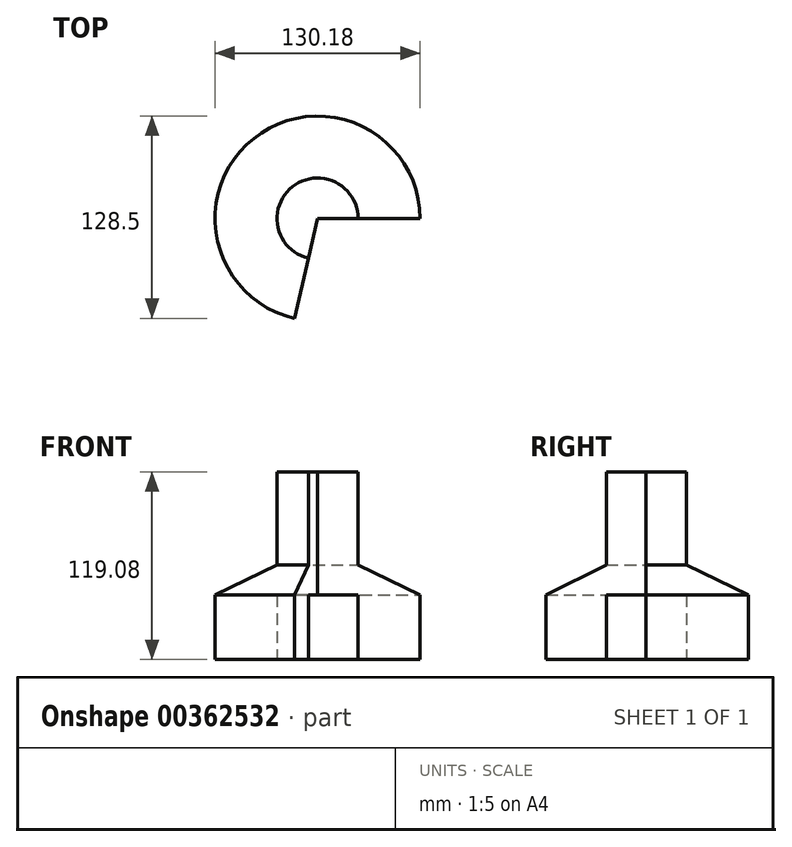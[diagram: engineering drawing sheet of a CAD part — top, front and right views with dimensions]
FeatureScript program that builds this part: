
annotation { "Feature Type Name" : "Feature", "Feature Type Description" : "" }
export const myFeature = defineFeature(function(context is Context, id is Id, definition is map)
    precondition{}
    {
        {
            var Q0;
            Q0=qCreatedBy(makeId("Front.planeOp"),FACE);
            var sketch = newSketch(context, id + "F0", { "sketchPlane" : qUnion([Q0])});
            skLineSegment(sketch, "E0", {"start": v(0, 58.94) * mm, "end": v(25.8, 58.94) * mm});
            skLineSegment(sketch, "E1", {"start": v(25.8, 58.94) * mm, "end": v(25.8, 0) * mm});
            skLineSegment(sketch, "E2", {"start": v(25.8, 0) * mm, "end": v(65.09, -19.28) * mm});
            skLineSegment(sketch, "E3", {"start": v(65.09, -60.14) * mm, "end": v(65.09, -19.28) * mm});
            skLineSegment(sketch, "E4", {"start": v(25.8, -60.14) * mm, "end": v(65.09, -60.14) * mm});
            skLineSegment(sketch, "E5", {"start": v(25.8, -60.14) * mm, "end": v(25.8, -19.28) * mm});
            skLineSegment(sketch, "E6", {"start": v(25.8, -19.28) * mm, "end": v(0, -19.28) * mm});
            skLineSegment(sketch, "E7", {"start": v(0, -19.28) * mm, "end": v(0, 58.94) * mm, "construction": true});
            skLineSegment(sketch, "E8", {"start": v(0, -19.28) * mm, "end": v(0, 58.94) * mm});
            skSolve(sketch);
        }
        {
            var Q0;
            Q0 = qSketchRegion(id + "F0", true);
            var Q1;
            Q1=sQuery(id+"F0.wireOp",EDGE,"E7");
            revolve(context, id + "F1", {"entities" : qUnion([Q0]), "axis" : qUnion([Q1]), "revolveType" : RevolveType.ONE_DIRECTION, "angle" : 256.96 * degree});
        }
    });
